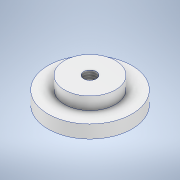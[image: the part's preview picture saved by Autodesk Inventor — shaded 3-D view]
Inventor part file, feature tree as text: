
AUTODESK INVENTOR PART (.ipt)
format: ipt  version: 2021 (Build 250183000, 183)  size: 114,176 bytes
history: native  units: in
note: dims shown in document units (in); Inventor stores cm internally (conversion verified against a paired STEP export)
features: sketch x3, extrude x2, hole x1
ambient origin geometry x8: Origin, YZ Plane, XZ Plane, XY Plane, X Axis, Y Axis, Z Axis, Center Point
bodies: Solid1 (feature_tree)
feature tree (6):
  extrude  "Extrusion1"  TaperAngle=0.0deg  [1 undecoded]
  extrude  "Extrusion2"  [1 undecoded]
  hole  "Hole1"  [1 undecoded]
  sketch  "Sketch1"  dims[d2=0.0in d5=0.0in]
  sketch  "Sketch2"  dims[d6=0.156in d7=0.25in d8=0.385in d9=0.25in d10=0.5635in d11=0.25in d12=0.0in]
  sketch  "Sketch3"
note: 3 required parameter values undecoded (feature->parameter linkage not recoverable at this tier; creation-order binding heuristic only, values carry confidence <= 0.55)
